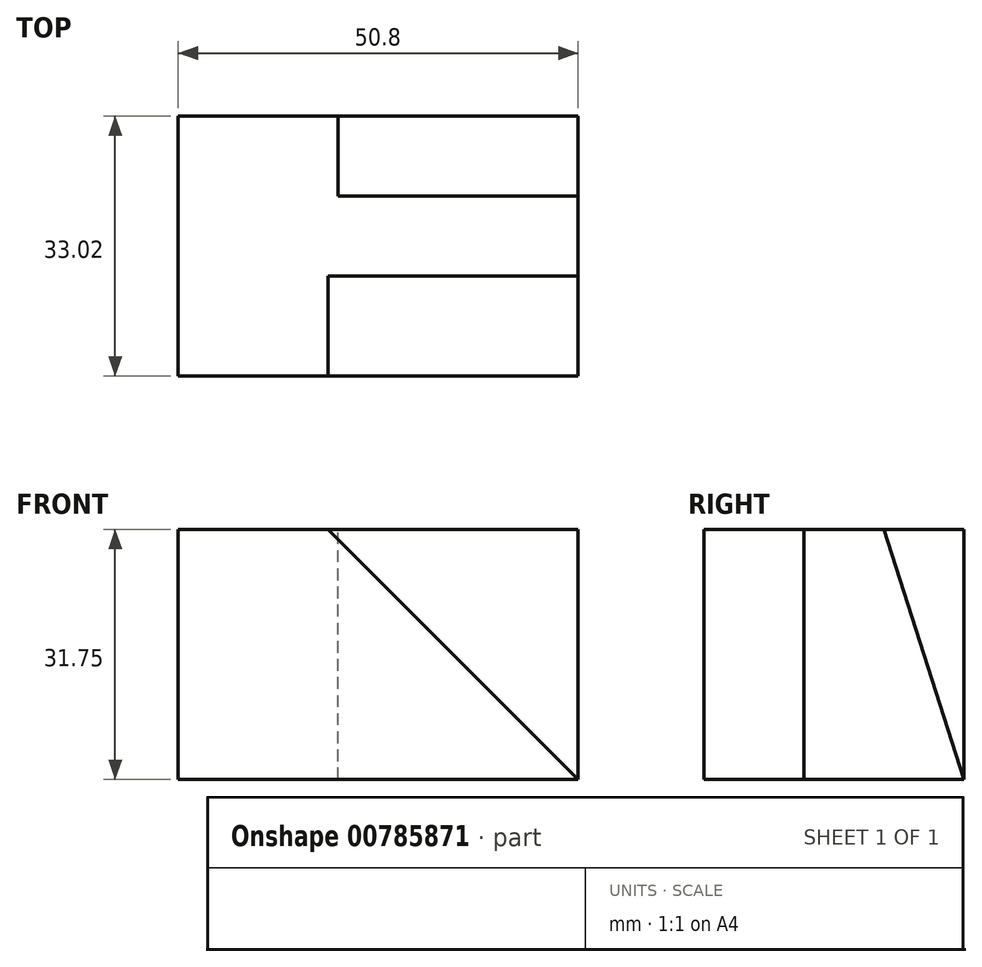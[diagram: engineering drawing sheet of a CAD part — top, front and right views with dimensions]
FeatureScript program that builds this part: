
annotation { "Feature Type Name" : "Feature", "Feature Type Description" : "" }
export const myFeature = defineFeature(function(context is Context, id is Id, definition is map)
    precondition{}
    {
        {
            var Q0;
            Q0=qCreatedBy(makeId("Front.planeOp"),FACE);
            var sketch = newSketch(context, id + "F0", { "sketchPlane" : qUnion([Q0])});
            skLineSegment(sketch, "E0", {"start": v(0, 0) * mm, "end": v(25.4, 0) * mm});
            skLineSegment(sketch, "E1", {"start": v(25.4, 0) * mm, "end": v(25.4, 31.75) * mm});
            skLineSegment(sketch, "E2", {"start": v(-25.4, 31.75) * mm, "end": v(25.4, 31.75) * mm});
            skLineSegment(sketch, "E3", {"start": v(-25.4, 31.75) * mm, "end": v(-25.4, 0) * mm});
            skLineSegment(sketch, "E4", {"start": v(-25.4, 0) * mm, "end": v(0, 0) * mm});
            skSolve(sketch);
        }
        {
            var Q0;
            Q0=makeQuery(id+"F0.imprint","IMPRINT",FACE,{"disambiguationData":[TD([[makeQuery(id+"F0.imprint","IMPRINT",EDGE,{"derivedFrom":sQuery(id+"F0.wireOp",EDGE,"E0")}),1.0]])]});
            extrude(context, id + "F1", {"entities" : qUnion([Q0]), "depth" : 33.02 * mm, "offsetDistance" : 25.4 * mm});
        }
        {
            var Q0;
            Q0=makeQuery(id+"F1.opExtrude","CAP_FACE",FACE,{"disambiguationData":[OSD([sQuery(id+"F0.wireOp",EDGE,"E0"),sQuery(id+"F0.wireOp",EDGE,"E1"),sQuery(id+"F0.wireOp",EDGE,"E2"),sQuery(id+"F0.wireOp",EDGE,"E3"),sQuery(id+"F0.wireOp",EDGE,"E4")])],"isStart":false});
            var sketch = newSketch(context, id + "F2", { "sketchPlane" : qUnion([Q0])});
            skLineSegment(sketch, "E5", {"start": v(-6.36, 31.75) * mm, "end": v(-25.4, 31.75) * mm});
            skLineSegment(sketch, "E6", {"start": v(-25.4, 31.75) * mm, "end": v(-6.36, 31.75) * mm});
            skLineSegment(sketch, "E7", {"start": v(-6.36, 31.75) * mm, "end": v(25.4, 0) * mm});
            skSolve(sketch);
        }
        {
            var Q0;
            {var subQ0=sQuery(id+"F2.wireOp",EDGE,"E7");Q0=makeQuery(id+"F2.imprint","IMPRINT",FACE,{"disambiguationData":[TD([[makeQuery(id+"F2.imprint","IMPRINT",EDGE,{"derivedFrom":subQ0}),1.0]])]});}
            extrude(context, id + "F3", {"entities" : qUnion([Q0]), "operationType" : NewBodyOperationType.REMOVE, "oppositeDirection" : true, "depth" : 12.7 * mm, "offsetDistance" : 25.4 * mm});
        }
        {
            var Q0;
            Q0=makeQuery(id+"F1.opExtrude","SWEPT_FACE",FACE,{"disambiguationData":[OSD([sQuery(id+"F0.wireOp",EDGE,"E1")])]});
            var sketch = newSketch(context, id + "F4", { "sketchPlane" : qUnion([Q0])});
            skLineSegment(sketch, "E8", {"start": v(0, 0) * mm, "end": v(-10.16, 31.75) * mm});
            skSolve(sketch);
        }
        {
            var Q0;
            {var subQ0=sQuery(id+"F4.wireOp",EDGE,"E8");Q0=makeQuery(id+"F4.imprint","IMPRINT",FACE,{"disambiguationData":[TD([[makeQuery(id+"F4.imprint","IMPRINT",EDGE,{"derivedFrom":subQ0}),-1.0]])]});}
            extrude(context, id + "F5", {"entities" : qUnion([Q0]), "operationType" : NewBodyOperationType.REMOVE, "oppositeDirection" : true, "depth" : 30.48 * mm, "offsetDistance" : 25.4 * mm});
        }
    });
